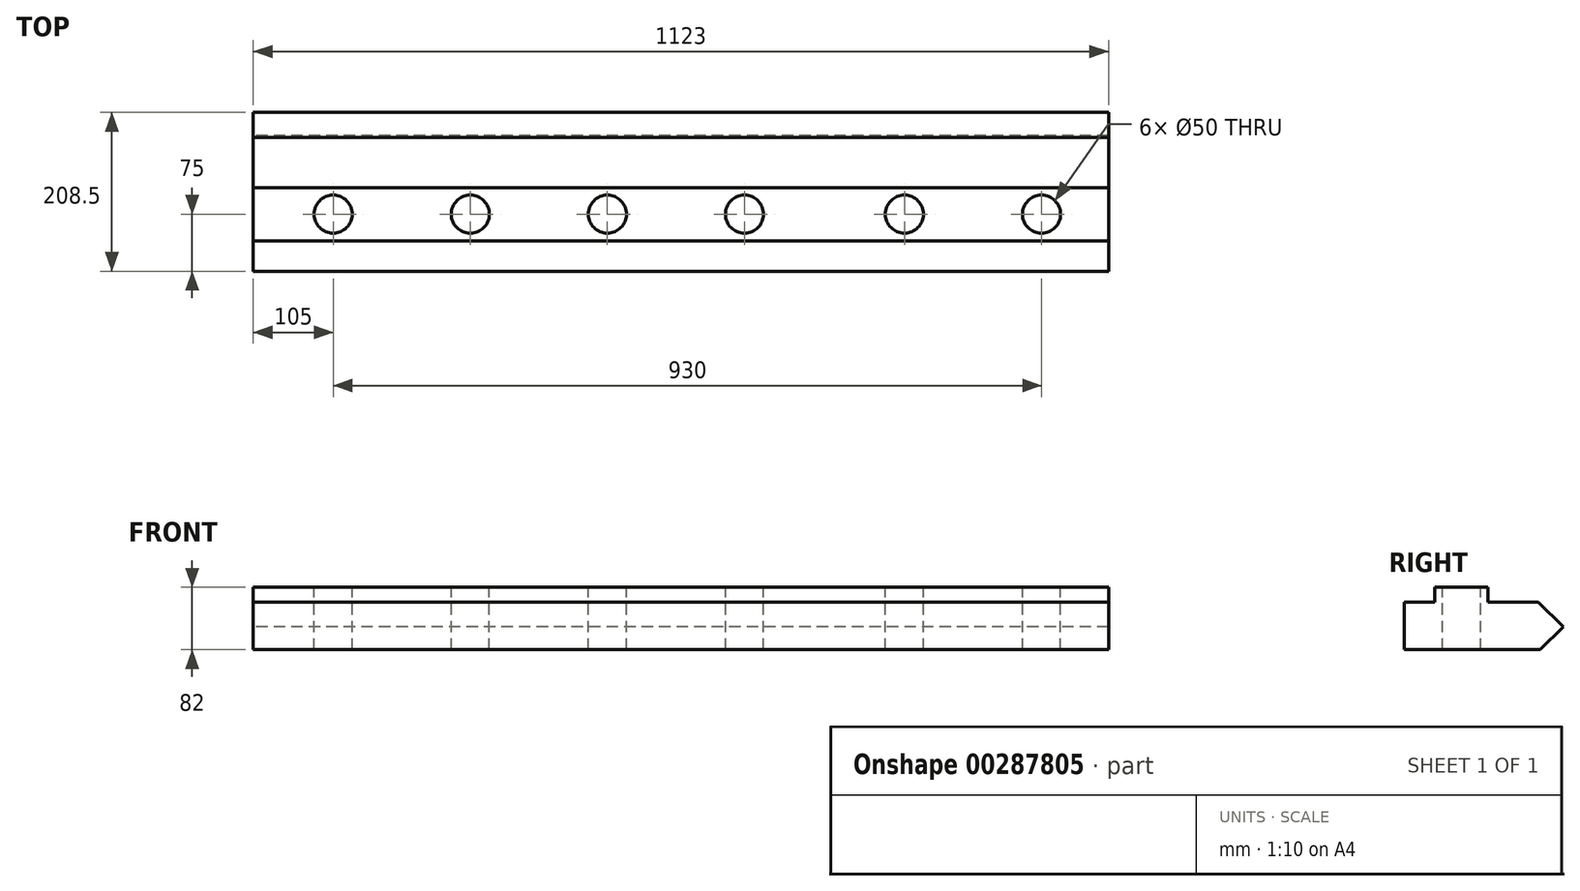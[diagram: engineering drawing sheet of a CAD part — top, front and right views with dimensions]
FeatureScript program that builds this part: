
annotation { "Feature Type Name" : "Feature", "Feature Type Description" : "" }
export const myFeature = defineFeature(function(context is Context, id is Id, definition is map)
    precondition{}
    {
        {
            var Q0;
            Q0=qCreatedBy(makeId("Right.planeOp"),FACE);
            var sketch = newSketch(context, id + "F0", { "sketchPlane" : qUnion([Q0])});
            skLineSegment(sketch, "E0.bottom", {"start": v(0, 0) * mm, "end": v(178.5, 0) * mm});
            skLineSegment(sketch, "E0.top", {"start": v(40, 82) * mm, "end": v(110, 82) * mm});
            skLineSegment(sketch, "E0.left", {"start": v(0, 0) * mm, "end": v(0, 62.5) * mm});
            skLineSegment(sketch, "E1", {"start": v(0, 62.5) * mm, "end": v(40, 62.5) * mm});
            skLineSegment(sketch, "E2", {"start": v(40, 62.5) * mm, "end": v(40, 82) * mm});
            skLineSegment(sketch, "E3", {"start": v(208.5, 30) * mm, "end": v(176, 62.5) * mm});
            skLineSegment(sketch, "E4", {"start": v(208.5, 30) * mm, "end": v(178.5, 0) * mm});
            skLineSegment(sketch, "E5", {"start": v(110, 82) * mm, "end": v(110, 62.5) * mm});
            skLineSegment(sketch, "E6", {"start": v(110, 62.5) * mm, "end": v(176, 62.5) * mm});
            skLineSegment(sketch, "E7", {"start": v(208.5, 78.56) * mm, "end": v(208.5, -44.4) * mm, "construction": true});
            skSolve(sketch);
        }
        {
            var Q0;
            Q0=makeQuery(id+"F0.imprint","IMPRINT",FACE,{"disambiguationData":[TD([[makeQuery(id+"F0.imprint","IMPRINT",EDGE,{"derivedFrom":sQuery(id+"F0.wireOp",EDGE,"E0.bottom")}),1.0]])]});
            extrude(context, id + "F1", {"entities" : qUnion([Q0]), "endBound" : BoundingType.SYMMETRIC, "depth" : 1123 * mm});
        }
        {
            var Q0;
            Q0=makeQuery(id+"F1.opExtrude","SWEPT_FACE",FACE,{"disambiguationData":[OSD([sQuery(id+"F0.wireOp",EDGE,"E0.top")])]});
            var sketch = newSketch(context, id + "F2", { "sketchPlane" : qUnion([Q0])});
            skCircle(sketch, "E8", {"center": v(473.5, 75) * mm, "radius": 25 * mm});
            skLineSegment(sketch, "E9", {"start": v(561.5, 75) * mm, "end": v(-561.5, 75) * mm, "construction": true});
            skCircle(sketch, "E10.1.0.0", {"center": v(293.5, 75) * mm, "radius": 25 * mm});
            skCircle(sketch, "E10.2.0.0", {"center": v(83.5, 75) * mm, "radius": 25 * mm});
            skCircle(sketch, "E10.3.0.0", {"center": v(-96.5, 75) * mm, "radius": 25 * mm});
            skLineSegment(sketch, "E10.direction1", {"start": v(473.5, 75) * mm, "end": v(293.5, 75) * mm, "construction": true});
            skCircle(sketch, "E11.3.0.0", {"center": v(-276.5, 75) * mm, "radius": 25 * mm});
            skCircle(sketch, "E12.3.0.0", {"center": v(-456.5, 75) * mm, "radius": 25 * mm});
            skSolve(sketch);
        }
        {
            var Q0;
            Q0 = qSketchRegion(id + "F2", true);
            extrude(context, id + "F3", {"entities" : qUnion([Q0]), "operationType" : NewBodyOperationType.REMOVE, "endBound" : BoundingType.THROUGH_ALL, "oppositeDirection" : true, "depth" : 25 * mm});
        }
    });
